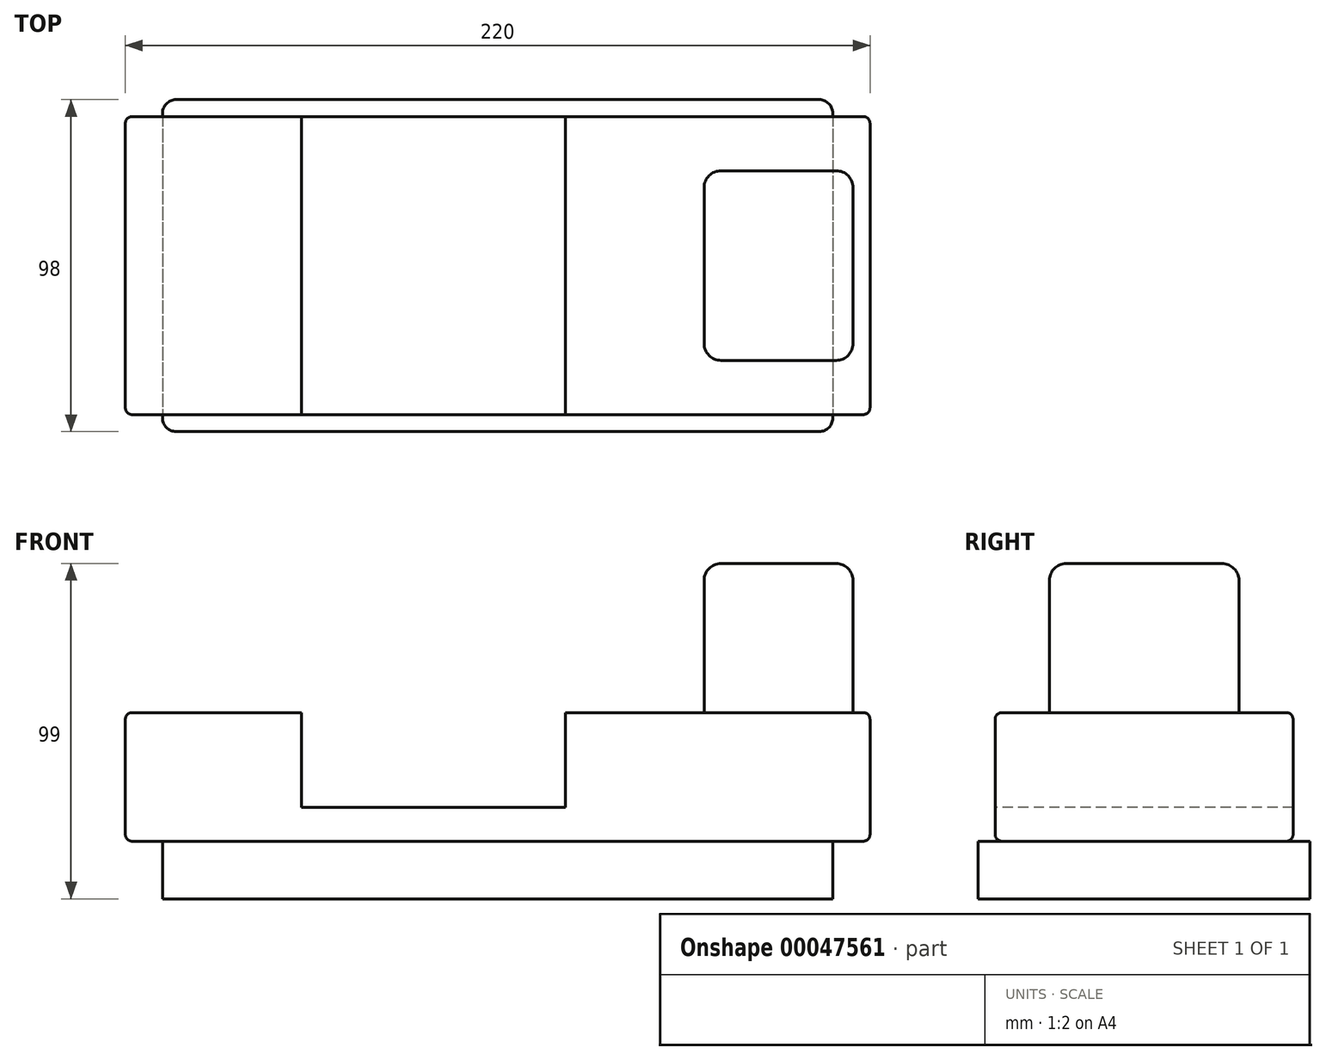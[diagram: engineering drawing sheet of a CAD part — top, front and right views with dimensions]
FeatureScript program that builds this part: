
annotation { "Feature Type Name" : "Feature", "Feature Type Description" : "" }
export const myFeature = defineFeature(function(context is Context, id is Id, definition is map)
    precondition{}
    {
        {
            assignVariable(context, id + "F0", {"name" : "cutdepth", "anyValue" : 28});
        }
        {
            var Q0;
            Q0=qCreatedBy(makeId("Top.planeOp"),FACE);
            var sketch = newSketch(context, id + "F1", { "sketchPlane" : qUnion([Q0])});
            skLineSegment(sketch, "E0.bottom", {"start": v(-89, 44.19) * mm, "end": v(109, 44.19) * mm});
            skLineSegment(sketch, "E0.top", {"start": v(-89, -53.81) * mm, "end": v(109, -53.81) * mm});
            skLineSegment(sketch, "E0.left", {"start": v(-89, 44.19) * mm, "end": v(-89, -53.81) * mm});
            skLineSegment(sketch, "E0.right", {"start": v(109, 44.19) * mm, "end": v(109, -53.81) * mm});
            skSolve(sketch);
        }
        {
            var Q0;
            Q0=qSketchRegion(id+"F1",true);
            extrude(context, id + "F2", {"entities" : qUnion([Q0]), "depth" : 17 * mm});
        }
        {
            var Q0;
            Q0=makeQuery(id+"F2.opExtrude","CAP_FACE",FACE,{"disambiguationData":[OSD([sQuery(id+"F1.wireOp",EDGE,"E0.bottom"),sQuery(id+"F1.wireOp",EDGE,"E0.top"),sQuery(id+"F1.wireOp",EDGE,"E0.left"),sQuery(id+"F1.wireOp",EDGE,"E0.right")])],"isStart":false});
            var sketch = newSketch(context, id + "F3", { "sketchPlane" : qUnion([Q0])});
            skLineSegment(sketch, "E1.bottom", {"start": v(-100, 39.19) * mm, "end": v(120, 39.19) * mm});
            skLineSegment(sketch, "E1.top", {"start": v(-100, -48.81) * mm, "end": v(120, -48.81) * mm});
            skLineSegment(sketch, "E1.left", {"start": v(-100, 39.19) * mm, "end": v(-100, -48.81) * mm});
            skLineSegment(sketch, "E1.right", {"start": v(120, 39.19) * mm, "end": v(120, -48.81) * mm});
            skLineSegment(sketch, "E2", {"start": v(10, -53.81) * mm, "end": v(10, 44.19) * mm, "construction": true});
            skLineSegment(sketch, "E3", {"start": v(-89, -4.81) * mm, "end": v(109, -4.81) * mm, "construction": true});
            skLineSegment(sketch, "E4", {"start": v(120, -48.81) * mm, "end": v(-100, 39.19) * mm, "construction": true});
            skLineSegment(sketch, "E5", {"start": v(-100, -48.81) * mm, "end": v(120, 39.19) * mm, "construction": true});
            skPoint(sketch, "E6", {"position": v(10, -4.81) * mm});
            skSolve(sketch);
        }
        {
            var Q0;
            Q0=qSketchRegion(id+"F3",true);
            extrude(context, id + "F4", {"entities" : qUnion([Q0]), "depth" : 38 * mm});
        }
        {
            var Q0;
            Q0=makeQuery(id+"F4.opExtrude","CAP_FACE",FACE,{"disambiguationData":[OSD([sQuery(id+"F3.wireOp",EDGE,"E1.bottom"),sQuery(id+"F3.wireOp",EDGE,"E1.top"),sQuery(id+"F3.wireOp",EDGE,"E1.left"),sQuery(id+"F3.wireOp",EDGE,"E1.right")])],"isStart":false});
            var sketch = newSketch(context, id + "F5", { "sketchPlane" : qUnion([Q0])});
            skLineSegment(sketch, "E7", {"start": v(93, 39.19) * mm, "end": v(93, -48.81) * mm, "construction": true});
            skPoint(sketch, "E8", {"position": v(93, -4.81) * mm});
            skLineSegment(sketch, "E9.bottom", {"start": v(115, 23.19) * mm, "end": v(71, 23.19) * mm});
            skLineSegment(sketch, "E9.top", {"start": v(115, -32.81) * mm, "end": v(71, -32.81) * mm});
            skLineSegment(sketch, "E9.left", {"start": v(115, 23.19) * mm, "end": v(115, -32.81) * mm});
            skLineSegment(sketch, "E9.right", {"start": v(71, 23.19) * mm, "end": v(71, -32.81) * mm});
            skLineSegment(sketch, "E10", {"start": v(115, 23.19) * mm, "end": v(71, -32.81) * mm, "construction": true});
            skSolve(sketch);
        }
        {
            var Q0;
            Q0=qSketchRegion(id+"F5",true);
            extrude(context, id + "F6", {"entities" : qUnion([Q0]), "depth" : 44 * mm});
        }
        {
            var Q0;
            Q0=makeQuery(id+"F4.opExtrude","CAP_FACE",FACE,{"disambiguationData":[OSD([sQuery(id+"F3.wireOp",EDGE,"E1.bottom"),sQuery(id+"F3.wireOp",EDGE,"E1.top"),sQuery(id+"F3.wireOp",EDGE,"E1.left"),sQuery(id+"F3.wireOp",EDGE,"E1.right")])],"isStart":false});
            var sketch = newSketch(context, id + "F7", { "sketchPlane" : qUnion([Q0])});
            skLineSegment(sketch, "E11.bottom", {"start": v(-48, 40.7) * mm, "end": v(30, 40.7) * mm});
            skLineSegment(sketch, "E11.top", {"start": v(-48, -49.3) * mm, "end": v(30, -49.3) * mm});
            skLineSegment(sketch, "E11.left", {"start": v(-48, 40.7) * mm, "end": v(-48, -49.3) * mm});
            skLineSegment(sketch, "E11.right", {"start": v(30, 40.7) * mm, "end": v(30, -49.3) * mm});
            skSolve(sketch);
        }
        {
            var Q0;
            Q0=qSketchRegion(id+"F7",true);
            extrude(context, id + "F8", {"entities" : qUnion([Q0]), "operationType" : NewBodyOperationType.REMOVE, "oppositeDirection" : true, "depth" : getVariable(context, 'cutdepth') * mm});
        }
        {
            var Q0;
            {var subQ0=sQuery(id+"F3.wireOp",EDGE,"E1.top");var subQ1=sQuery(id+"F3.wireOp",EDGE,"E1.left");Q0=makeQuery(id+"F8.boolean.opBoolean","SPLIT",EDGE,{"disambiguationData":[TD([makeQuery(id+"F4.opExtrude","SWEPT_FACE",FACE,{"disambiguationData":[OSD([subQ1])]})])],"derivedFrom":makeQuery(id+"F4.opExtrude","CAP_EDGE",EDGE,{"disambiguationData":[OSD([subQ0])],"isStart":false})});}
            var Q1;
            {var subQ0=sQuery(id+"F3.wireOp",EDGE,"E1.bottom");var subQ1=sQuery(id+"F3.wireOp",EDGE,"E1.left");Q1=makeQuery(id+"F8.boolean.opBoolean","SPLIT",EDGE,{"disambiguationData":[TD([makeQuery(id+"F4.opExtrude","SWEPT_FACE",FACE,{"disambiguationData":[OSD([subQ1])]})])],"derivedFrom":makeQuery(id+"F4.opExtrude","CAP_EDGE",EDGE,{"disambiguationData":[OSD([subQ0])],"isStart":false})});}
            var Q2;
            {var subQ0=sQuery(id+"F3.wireOp",EDGE,"E1.top");var subQ1=sQuery(id+"F3.wireOp",EDGE,"E1.right");Q2=makeQuery(id+"F8.boolean.opBoolean","SPLIT",EDGE,{"disambiguationData":[TD([makeQuery(id+"F4.opExtrude","SWEPT_FACE",FACE,{"disambiguationData":[OSD([subQ1])]})])],"derivedFrom":makeQuery(id+"F4.opExtrude","CAP_EDGE",EDGE,{"disambiguationData":[OSD([subQ0])],"isStart":false})});}
            var Q3;
            Q3=makeQuery(id+"F4.opExtrude","CAP_EDGE",EDGE,{"disambiguationData":[OSD([sQuery(id+"F3.wireOp",EDGE,"E1.top")])],"isStart":true});
            var Q4;
            {var subQ0=sQuery(id+"F3.wireOp",EDGE,"E1.bottom");var subQ1=sQuery(id+"F3.wireOp",EDGE,"E1.right");Q4=makeQuery(id+"F8.boolean.opBoolean","SPLIT",EDGE,{"disambiguationData":[TD([makeQuery(id+"F4.opExtrude","SWEPT_FACE",FACE,{"disambiguationData":[OSD([subQ1])]})])],"derivedFrom":makeQuery(id+"F4.opExtrude","CAP_EDGE",EDGE,{"disambiguationData":[OSD([subQ0])],"isStart":false})});}
            var Q5;
            Q5=makeQuery(id+"F4.opExtrude","CAP_EDGE",EDGE,{"disambiguationData":[OSD([sQuery(id+"F3.wireOp",EDGE,"E1.bottom")])],"isStart":true});
            var Q6;
            Q6=makeQuery(id+"F4.opExtrude","CAP_EDGE",EDGE,{"disambiguationData":[OSD([sQuery(id+"F3.wireOp",EDGE,"E1.left")])],"isStart":false});
            var Q7;
            Q7=makeQuery(id+"F4.opExtrude","SWEPT_EDGE",EDGE,{"disambiguationData":[OSD([sQuery(id+"F3.wireOp",EDGE,"E1.top"),sQuery(id+"F3.wireOp",EDGE,"E1.left")])]});
            var Q8;
            Q8=makeQuery(id+"F4.opExtrude","CAP_EDGE",EDGE,{"disambiguationData":[OSD([sQuery(id+"F3.wireOp",EDGE,"E1.left")])],"isStart":true});
            var Q9;
            Q9=makeQuery(id+"F4.opExtrude","SWEPT_EDGE",EDGE,{"disambiguationData":[OSD([sQuery(id+"F3.wireOp",EDGE,"E1.bottom"),sQuery(id+"F3.wireOp",EDGE,"E1.left")])]});
            var Q10;
            Q10=makeQuery(id+"F4.opExtrude","SWEPT_EDGE",EDGE,{"disambiguationData":[OSD([sQuery(id+"F3.wireOp",EDGE,"E1.top"),sQuery(id+"F3.wireOp",EDGE,"E1.right")])]});
            var Q11;
            Q11=makeQuery(id+"F4.opExtrude","CAP_EDGE",EDGE,{"disambiguationData":[OSD([sQuery(id+"F3.wireOp",EDGE,"E1.right")])],"isStart":false});
            var Q12;
            Q12=makeQuery(id+"F4.opExtrude","CAP_EDGE",EDGE,{"disambiguationData":[OSD([sQuery(id+"F3.wireOp",EDGE,"E1.right")])],"isStart":true});
            var Q13;
            Q13=makeQuery(id+"F4.opExtrude","SWEPT_EDGE",EDGE,{"disambiguationData":[OSD([sQuery(id+"F3.wireOp",EDGE,"E1.bottom"),sQuery(id+"F3.wireOp",EDGE,"E1.right")])]});
            fillet(context, id + "F9", {"entities" : qUnion([Q0, Q1, Q2, Q3, Q4, Q5, Q6, Q7, Q8, Q9, Q10, Q11, Q12, Q13]), "radius" : 2 * mm, "tangentPropagation" : true, "allowEdgeOverflow" : false});
        }
        {
            var Q0;
            Q0=makeQuery(id+"F2.opExtrude","SWEPT_EDGE",EDGE,{"disambiguationData":[OSD([sQuery(id+"F1.wireOp",EDGE,"E0.top"),sQuery(id+"F1.wireOp",EDGE,"E0.left")])]});
            var Q1;
            Q1=makeQuery(id+"F2.opExtrude","SWEPT_EDGE",EDGE,{"disambiguationData":[OSD([sQuery(id+"F1.wireOp",EDGE,"E0.top"),sQuery(id+"F1.wireOp",EDGE,"E0.right")])]});
            var Q2;
            Q2=makeQuery(id+"F2.opExtrude","SWEPT_EDGE",EDGE,{"disambiguationData":[OSD([sQuery(id+"F1.wireOp",EDGE,"E0.bottom"),sQuery(id+"F1.wireOp",EDGE,"E0.right")])]});
            var Q3;
            Q3=makeQuery(id+"F2.opExtrude","SWEPT_EDGE",EDGE,{"disambiguationData":[OSD([sQuery(id+"F1.wireOp",EDGE,"E0.bottom"),sQuery(id+"F1.wireOp",EDGE,"E0.left")])]});
            fillet(context, id + "F10", {"entities" : qUnion([Q0, Q1, Q2, Q3]), "radius" : 4 * mm, "tangentPropagation" : true, "allowEdgeOverflow" : false});
        }
        {
            var Q0;
            Q0=makeQuery(id+"F6.opExtrude","CAP_EDGE",EDGE,{"disambiguationData":[OSD([sQuery(id+"F5.wireOp",EDGE,"E9.top")])],"isStart":false});
            var Q1;
            Q1=makeQuery(id+"F6.opExtrude","CAP_EDGE",EDGE,{"disambiguationData":[OSD([sQuery(id+"F5.wireOp",EDGE,"E9.left")])],"isStart":false});
            var Q2;
            Q2=makeQuery(id+"F6.opExtrude","CAP_EDGE",EDGE,{"disambiguationData":[OSD([sQuery(id+"F5.wireOp",EDGE,"E9.bottom")])],"isStart":false});
            var Q3;
            Q3=makeQuery(id+"F6.opExtrude","CAP_EDGE",EDGE,{"disambiguationData":[OSD([sQuery(id+"F5.wireOp",EDGE,"E9.right")])],"isStart":false});
            var Q4;
            Q4=makeQuery(id+"F6.opExtrude","SWEPT_EDGE",EDGE,{"disambiguationData":[OSD([sQuery(id+"F5.wireOp",EDGE,"E9.top"),sQuery(id+"F5.wireOp",EDGE,"E9.left")])]});
            var Q5;
            Q5=makeQuery(id+"F6.opExtrude","SWEPT_EDGE",EDGE,{"disambiguationData":[OSD([sQuery(id+"F5.wireOp",EDGE,"E9.top"),sQuery(id+"F5.wireOp",EDGE,"E9.right")])]});
            var Q6;
            Q6=makeQuery(id+"F6.opExtrude","SWEPT_EDGE",EDGE,{"disambiguationData":[OSD([sQuery(id+"F5.wireOp",EDGE,"E9.bottom"),sQuery(id+"F5.wireOp",EDGE,"E9.left")])]});
            var Q7;
            Q7=makeQuery(id+"F6.opExtrude","SWEPT_EDGE",EDGE,{"disambiguationData":[OSD([sQuery(id+"F5.wireOp",EDGE,"E9.bottom"),sQuery(id+"F5.wireOp",EDGE,"E9.right")])]});
            fillet(context, id + "F11", {"entities" : qUnion([Q0, Q1, Q2, Q3, Q4, Q5, Q6, Q7]), "radius" : 5 * mm, "tangentPropagation" : true, "allowEdgeOverflow" : false});
        }
    });
